# Revit family: POOL SPOT LINEAL 18W_U2418SW.2.30
name_source: partatom
category: Luminarias
units: mm (PartAtom-declared; Revit-internal decimal feet)

## family parameters
Compartido = No
Corte con vacíos al cargar = No
Cota de conector redondo = Diámetro de uso
Origen de luz = Sí
Punto de cálculo de habitación = No
Se basa en plano de trabajo = Sí
Siempre vertical = No
Tipo de pieza = Normal

## types (1)
- SUB_U2418SW.2.30
    Cambio de temperatura de color de luz atenuada = <Ninguno>
    Comentarios de vataje = 24V
    Descripción = LUMINARIA SUB ACUATICA TIPO LINEAL, MIDIENDO 326MM DE LARGO POR 100MM INCLUYENDO ALETA PARA DIRIGIR, ACABADO EN ACERO INOXIDABLE, SELLO EN SILICON Y CUERPO MOLDEADO EN CROMO, 6 LED TIPO NICHIA CON UN CONSUMO TOTAL DE 22.8W, 1324 LUMENES, IP 68, IRC 80, IK 10, SUMERGIBLE MAXIMO 2M, CABLE H05RN DE 3M, APERTURA EN STOCK A 30 GRADOS, ALIMENTADA A 24V. REQUIERE ACCESORIOS.
    Elevación por defecto = 0 mm  [stored 0 ft]
    Fabricante = BRILLANT
    Filtro de color = 16777215
    Longitud de línea de emisión = 610 mm
    Longitud de símbolo de origen de luz = 500 mm  [stored 1.64042 ft]
    Lámpara = NICHIA
    Modelo = U2418SW.2.30
    Watt per fixture = 22.8
    Ángulo de campo de foco = 30.00°
    Ángulo de enfoque = 30.00°
    Ángulo de inclinación = 60.00°

note: [stored X ft] marks values corroborated as IEEE doubles in the binary element streams (Revit-internal decimal feet)

## geometry (parser evidence)
native form markers: Blend x2
no freeform markers — native parametric forms only
